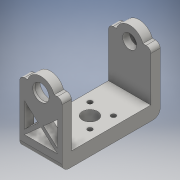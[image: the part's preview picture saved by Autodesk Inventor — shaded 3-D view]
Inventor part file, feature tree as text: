
AUTODESK INVENTOR PART (.ipt)
format: ipt  version: 2016 (Build 200138000, 138)  size: 290,304 bytes
history: native  units: mm
features: extrude x9, sketch x9, fillet x2, other x1
ambient origin geometry x8: Origin, YZ Plane, XZ Plane, XY Plane, X Axis, Y Axis, Z Axis, Center Point
bodies: Body1 (feature_tree)
feature tree (21):
  other  "ソリッド1"
  extrude  "押し出し1"  Depth=18.0mm
  extrude  "押し出し2"  Depth=41.8mm
  extrude  "押し出し3"  Depth=6.5mm
  extrude  "押し出し4"  Depth=10.0mm
  extrude  "押し出し5"  Depth=10.0mm
  extrude  "押し出し6"  Depth=2.0mm
  extrude  "押し出し7"  Depth=2.0mm
  extrude  "押し出し8"  Depth=2.0mm
  fillet  "フィレット1"  Radius=2.0mm
  fillet  "フィレット2"  Radius=6.0mm
  extrude  "押し出し9"  Depth=4.0mm
  sketch  "スケッチ1"
  sketch  "スケッチ2"
  sketch  "スケッチ3"
  sketch  "スケッチ4"
  sketch  "スケッチ5"
  sketch  "スケッチ6"
  sketch  "スケッチ7"
  sketch  "スケッチ8"
  sketch  "スケッチ9"
